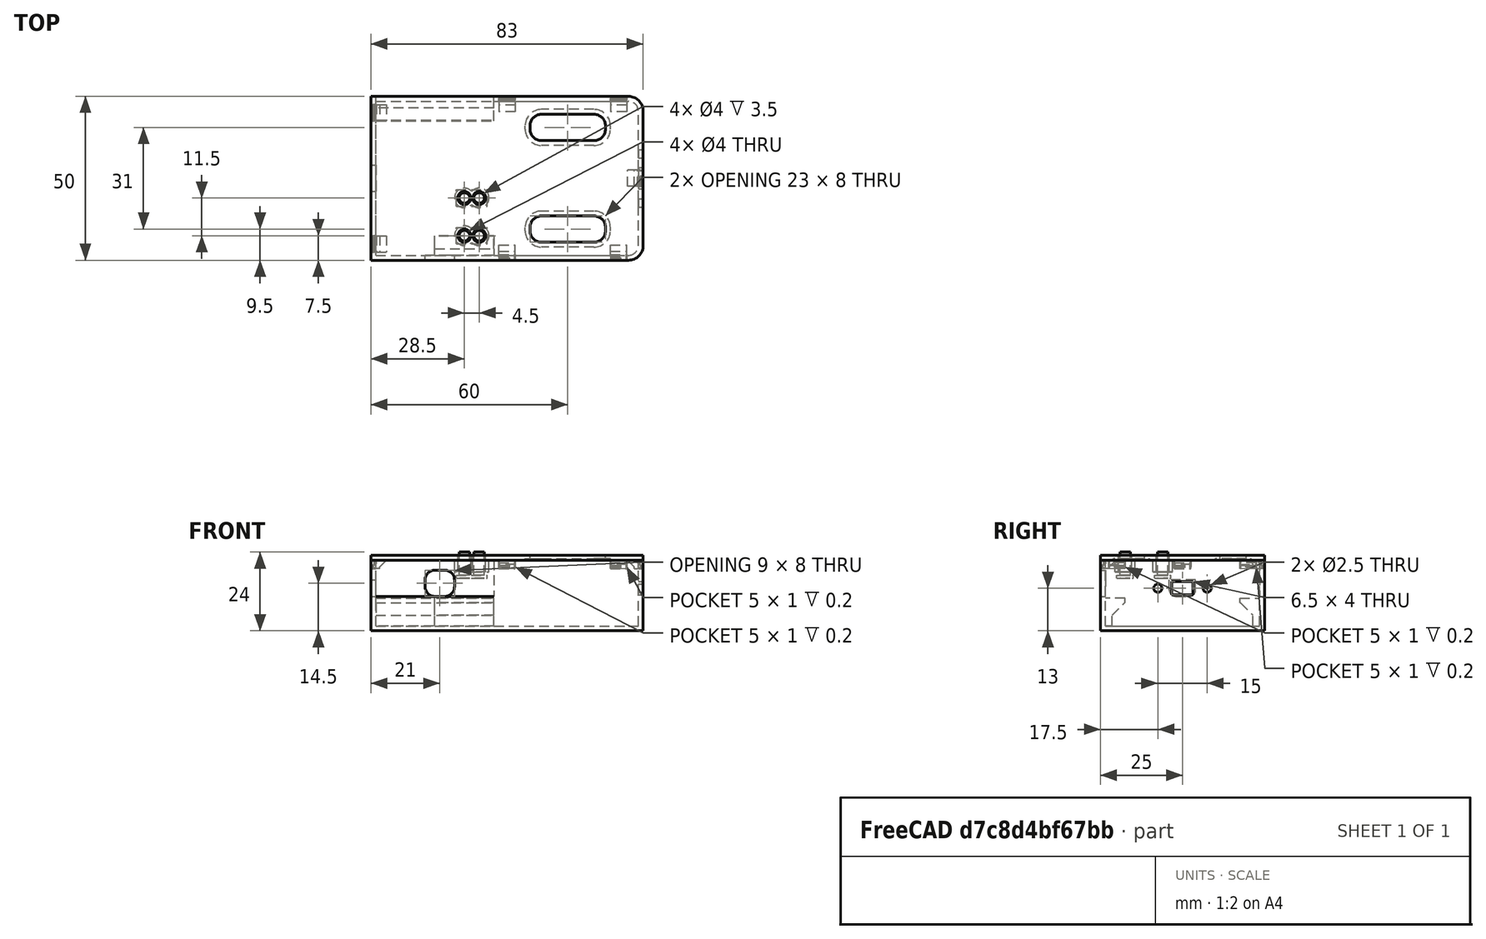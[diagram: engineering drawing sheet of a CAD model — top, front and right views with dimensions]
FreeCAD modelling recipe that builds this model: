
FCSTD DOCUMENT  (FreeCAD 0.19R24291 (Git))
Label: mp3-player
License: All rights reserved
LicenseURL: http://en.wikipedia.org/wiki/All_rights_reserved
objects: Part::Box×46, Part::Cut×36, Part::Chamfer×29, Part::Fuse×22, Part::Cylinder×18, Part::Fillet×16, Part::MultiFuse×1
note: 168 computed .brp shape members not serialized (recipe doc carries the construction recipe); baked Part::Feature solids carry a one-line shape summary decoded from their .brp

FEATURE [Part::Box] Box  label="Cube"
  AttacherType = Attacher::AttachEngine3D
  Height = 20
  Length = 80
  Placement = pos=(0,0,1.5) rot=(0,0,1;0rad)
  Width = 47
FEATURE [Part::Box] Box001  label="Cube001"
  AttacherType = Attacher::AttachEngine3D
  Height = 21.5
  Length = 83
  Placement = pos=(-1.5,-1.5,0) rot=(0,0,1;0rad)
  Width = 50
FEATURE [Part::Box] Box002  label="Cube002"
  AttacherType = Attacher::AttachEngine3D
  Height = 11
  Length = 36
  Placement = pos=(0,8,10.5) rot=(0,0,1;0rad)
  Width = 47
FEATURE [Part::Cut] Cut
  Base = -> Box001
  Tool = -> Box
FEATURE [Part::Fillet] Fillet
  Base = -> Cut
  Edges = 2 edges r=3: [Edge21,Edge22]
FEATURE [Part::Fillet] Fillet001
  Base = -> Fillet
  Edges = 2 edges r=4.5: [Edge27,Edge29]
FEATURE [Part::Box] Box003  label="Cube003"
  AttacherType = Attacher::AttachEngine3D
  Height = 5
  Length = 36
  Placement = pos=(-19,19.5,10.5) rot=(0,0,1;0rad)
  Width = 8
FEATURE [Part::Cut] Cut001
  Base = -> Fillet001
  Tool = -> Box002
FEATURE [Part::Cut] Cut002
  Base = -> Cut001
  Tool = -> Box003
FEATURE [Part::Fillet] Fillet002
  Base = -> Cut002
  Edges = 2 edges r=2: [Edge60,Edge61]
FEATURE [Part::Box] Box005  label="Cube005"
  AttacherType = Attacher::AttachEngine3D
  Height = 4
  Length = 10
  Placement = pos=(76,20.25,11) rot=(0,0,1;0rad)
  Width = 6.5
FEATURE [Part::Cylinder] Cylinder
  Angle = 360
  AttacherType = Attacher::AttachEngine3D
  Height = 10
  Placement = pos=(76,16,13) rot=(0,1,0;1.5708rad)
  Radius = 1.25
FEATURE [Part::Cylinder] Cylinder001
  Angle = 360
  AttacherType = Attacher::AttachEngine3D
  Height = 10
  Placement = pos=(76,31,13) rot=(0,1,0;1.5708rad)
  Radius = 1.25
FEATURE [Part::Cut] Cut003
  Base = -> Fillet002
  Tool = -> Cylinder
FEATURE [Part::Cut] Cut004
  Base = -> Cut003
  Tool = -> Cylinder001
FEATURE [Part::Cut] Cut005
  Base = -> Cut004
  Tool = -> Box005
FEATURE [Part::Box] Box006  label="Cube006"
  AttacherType = Attacher::AttachEngine3D
  Height = 1
  Length = 1
  Placement = pos=(-1,1,19) rot=(0,0,1;0rad)
  Width = 5
FEATURE [Part::Box] Box007  label="Cube007"
  AttacherType = Attacher::AttachEngine3D
  Height = 1
  Length = 1
  Placement = pos=(-1,41,19) rot=(0,0,1;0rad)
  Width = 5
FEATURE [Part::Box] Box008  label="Cube008"
  AttacherType = Attacher::AttachEngine3D
  Height = 1
  Length = 1
  Placement = pos=(80,21,19) rot=(0,0,1;0rad)
  Width = 5
FEATURE [Part::Box] Box009  label="Cube009"
  AttacherType = Attacher::AttachEngine3D
  Height = 1
  Length = 1
  Placement = pos=(37.5,1.1e-14,19) rot=(0,0,-1;1.5708rad)
  Width = 5
FEATURE [Part::Box] Box010  label="Cube010"
  AttacherType = Attacher::AttachEngine3D
  Height = 1
  Length = 1
  Placement = pos=(37.5,48,19) rot=(0,0,-1;1.5708rad)
  Width = 5
FEATURE [Part::Box] Box011  label="Cube011"
  AttacherType = Attacher::AttachEngine3D
  Height = 1
  Length = 1
  Placement = pos=(71.5,48,19) rot=(0,0,-1;1.5708rad)
  Width = 5
FEATURE [Part::Box] Box012  label="Cube012"
  AttacherType = Attacher::AttachEngine3D
  Height = 1
  Length = 1
  Placement = pos=(71.5,2.1e-14,19) rot=(0,0,-1;1.5708rad)
  Width = 5
FEATURE [Part::Box] Box013  label="Cube013"
  AttacherType = Attacher::AttachEngine3D
  Height = 3
  Length = 0.5
  Placement = pos=(71.5,2.1e-14,19) rot=(0,0,-1;1.5708rad)
  Width = 5
FEATURE [Part::Cut] Cut006
  Base = -> Cut005
  Tool = -> Box006
FEATURE [Part::Cut] Cut007
  Base = -> Cut006
  Tool = -> Box007
FEATURE [Part::Cut] Cut008
  Base = -> Cut007
  Tool = -> Box008
FEATURE [Part::Cut] Cut009
  Base = -> Cut008
  Tool = -> Box009
FEATURE [Part::Cut] Cut010
  Base = -> Cut009
  Tool = -> Box010
FEATURE [Part::Cut] Cut011
  Base = -> Cut010
  Tool = -> Box011
FEATURE [Part::Cut] Cut012
  Base = -> Cut011
  Tool = -> Box012
FEATURE [Part::Chamfer] Chamfer
  Base = -> Cut012
  Edges = 2 edges r=0.8: [Edge59,Edge79]
FEATURE [Part::Chamfer] Chamfer001
  Base = -> Chamfer
  Edges = 1 edges r=0.8: [Edge40]
FEATURE [Part::Chamfer] Chamfer002
  Base = -> Chamfer001
  Edges = 1 edges r=0.8: [Edge101]
FEATURE [Part::Chamfer] Chamfer003
  Base = -> Chamfer002
  Edges = 1 edges r=0.8: [Edge13]
FEATURE [Part::Chamfer] Chamfer004
  Base = -> Chamfer003
  Edges = 1 edges r=0.8: [Edge89]
FEATURE [Part::Chamfer] Chamfer005
  Base = -> Chamfer004
  Edges = 1 edges r=0.8: [Edge111]
FEATURE [Part::Box] Box015  label="Cube015"
  AttacherType = Attacher::AttachEngine3D
  Height = 3
  Length = 0.5
  Placement = pos=(37.5,1.3e-14,19) rot=(0,0,-1;1.5708rad)
  Width = 5
FEATURE [Part::Box] Box016  label="Cube016"
  AttacherType = Attacher::AttachEngine3D
  Height = 3
  Length = 0.5
  Placement = pos=(71.5,47.5,19) rot=(0,0,-1;1.5708rad)
  Width = 5
FEATURE [Part::Box] Box017  label="Cube017"
  AttacherType = Attacher::AttachEngine3D
  Height = 3
  Length = 0.5
  Placement = pos=(37.5,47.5,19) rot=(0,0,-1;1.5708rad)
  Width = 5
FEATURE [Part::Box] Box018  label="Cube018"
  AttacherType = Attacher::AttachEngine3D
  Height = 3
  Length = 0.5
  Placement = pos=(80,21,19) rot=(0,0,1;0rad)
  Width = 5
FEATURE [Part::Box] Box019  label="Cube019"
  AttacherType = Attacher::AttachEngine3D
  Height = 3
  Length = 0.5
  Placement = pos=(-0.5,41,19) rot=(0,0,1;0rad)
  Width = 5
FEATURE [Part::Box] Box020  label="Cube020"
  AttacherType = Attacher::AttachEngine3D
  Height = 3
  Length = 0.5
  Placement = pos=(-0.5,1,19) rot=(0,0,1;0rad)
  Width = 5
FEATURE [Part::Cut] Cut013
  Base = -> Chamfer005
  Tool = -> Box013
FEATURE [Part::Cut] Cut014
  Base = -> Cut013
  Tool = -> Box015
FEATURE [Part::Cut] Cut015
  Base = -> Cut014
  Tool = -> Box016
FEATURE [Part::Cut] Cut016
  Base = -> Cut015
  Tool = -> Box017
FEATURE [Part::Cut] Cut017
  Base = -> Cut016
  Tool = -> Box018
FEATURE [Part::Cut] Cut018
  Base = -> Cut017
  Tool = -> Box019
FEATURE [Part::Cut] Cut019
  Base = -> Cut018
  Tool = -> Box020
FEATURE [Part::Box] Box023  label="Cube023"
  AttacherType = Attacher::AttachEngine3D
  Height = 8
  Length = 9
  Placement = pos=(15,-6,10.5) rot=(0,0,1;0rad)
  Width = 47
FEATURE [Part::Cut] Cut020
  Base = -> Cut019
  Tool = -> Box023
FEATURE [Part::Fillet] Fillet003
  Base = -> Cut020
  Edges = 4 edges r=3: [Edge104,Edge105,Edge107,Edge109]
FEATURE [Part::Box] Box024  label="Cube024"
  AttacherType = Attacher::AttachEngine3D
  Height = 8.5
  Length = 36
  Placement = pos=(0,41,1.5) rot=(0,0,1;0rad)
  Width = 6
FEATURE [Part::Box] Box025  label="Cube025"
  AttacherType = Attacher::AttachEngine3D
  Height = 8.5
  Length = 36
  Placement = pos=(0,39,0) rot=(0,0,1;0rad)
  Width = 6
FEATURE [Part::Cut] Cut021
  Base = -> Box024
  Tool = -> Box025
FEATURE [Part::Box] Box026  label="Cube026"
  AttacherType = Attacher::AttachEngine3D
  Height = 8.5
  Length = 36
  Placement = pos=(0,41,1.5) rot=(0,0,1;0rad)
  Width = 6
FEATURE [Part::Box] Box027  label="Cube027"
  AttacherType = Attacher::AttachEngine3D
  Height = 8.5
  Length = 36
  Placement = pos=(0,39,0) rot=(0,0,1;0rad)
  Width = 6
FEATURE [Part::Cut] Cut022
  Base = -> Box026
  Placement = pos=(36,47,0) rot=(0,0,1;3.14159rad)
  Tool = -> Box027
FEATURE [Part::Box] Box028  label="Cube028"
  AttacherType = Attacher::AttachEngine3D
  Height = 11
  Length = 18
  Placement = pos=(0,-19.5,-0.5) rot=(0,0,1;0rad)
  Width = 47
FEATURE [Part::Cut] Cut023
  Base = -> Cut022
  Tool = -> Box028
FEATURE [Part::Box] Box014  label="Cube014"
  AttacherType = Attacher::AttachEngine3D
  Height = 0.8
  Length = 1
  Placement = pos=(71.5,0.2,19.1) rot=(0,0,-1;1.5708rad)
  Width = 5
FEATURE [Part::Box] Box029  label="Cube029"
  AttacherType = Attacher::AttachEngine3D
  Height = 1.5
  Length = 83
  Placement = pos=(-1.5,-1.5,21.5) rot=(0,0,1;0rad)
  Width = 50
FEATURE [Part::Fillet] Fillet004
  Base = -> Box029
  Edges = 2 edges r=4.5: [Edge5,Edge7]
FEATURE [Part::Box] Box030  label="Cube030"
  AttacherType = Attacher::AttachEngine3D
  Height = 3
  Length = 1
  Placement = pos=(71.5,1.2,19) rot=(0,0,-1;1.5708rad)
  Width = 5
FEATURE [Part::Fuse] Fusion
  Base = -> Box014
  Tool = -> Box030
FEATURE [Part::Chamfer] Chamfer006
  Base = -> Fusion
  Edges = 1 edges r=0.8: [Edge21]
FEATURE [Part::Chamfer] Chamfer007
  Base = -> Chamfer006
  Edges = 1 edges r=0.4: [Edge30]
FEATURE [Part::Box] Box031  label="Cube031"
  AttacherType = Attacher::AttachEngine3D
  Height = 3
  Length = 1
  Placement = pos=(71.5,1.2,19) rot=(0,0,-1;1.5708rad)
  Width = 5
FEATURE [Part::Box] Box032  label="Cube032"
  AttacherType = Attacher::AttachEngine3D
  Height = 0.8
  Length = 1
  Placement = pos=(71.5,0.2,19.1) rot=(0,0,-1;1.5708rad)
  Width = 5
FEATURE [Part::Fuse] Fusion001
  Base = -> Box032
  Tool = -> Box031
FEATURE [Part::Chamfer] Chamfer008
  Base = -> Fusion001
  Edges = 1 edges r=0.8: [Edge21]
FEATURE [Part::Chamfer] Chamfer009
  Base = -> Chamfer008
  Edges = 1 edges r=0.4: [Edge30]
  Placement = pos=(-34,0,0) rot=(0,0,1;0rad)
FEATURE [Part::Box] Box033  label="Cube033"
  AttacherType = Attacher::AttachEngine3D
  Height = 0.8
  Length = 1
  Placement = pos=(71.5,0.2,19.1) rot=(0,0,-1;1.5708rad)
  Width = 5
FEATURE [Part::Box] Box034  label="Cube034"
  AttacherType = Attacher::AttachEngine3D
  Height = 3
  Length = 1
  Placement = pos=(71.5,1.2,19) rot=(0,0,-1;1.5708rad)
  Width = 5
FEATURE [Part::Fuse] Fusion002
  Base = -> Box033
  Tool = -> Box034
FEATURE [Part::Chamfer] Chamfer010
  Base = -> Fusion002
  Edges = 1 edges r=0.8: [Edge21]
FEATURE [Part::Chamfer] Chamfer011
  Base = -> Chamfer010
  Edges = 1 edges r=0.4: [Edge30]
  Placement = pos=(114,47,0) rot=(0,0,1;3.14159rad)
FEATURE [Part::Box] Box035  label="Cube035"
  AttacherType = Attacher::AttachEngine3D
  Height = 3
  Length = 1
  Placement = pos=(71.5,1.2,19) rot=(0,0,-1;1.5708rad)
  Width = 5
FEATURE [Part::Box] Box036  label="Cube036"
  AttacherType = Attacher::AttachEngine3D
  Height = 0.8
  Length = 1
  Placement = pos=(71.5,0.2,19.1) rot=(0,0,-1;1.5708rad)
  Width = 5
FEATURE [Part::Fuse] Fusion003
  Base = -> Box036
  Tool = -> Box035
FEATURE [Part::Chamfer] Chamfer013
  Base = -> Fusion003
  Edges = 1 edges r=0.8: [Edge21]
FEATURE [Part::Chamfer] Chamfer012
  Base = -> Chamfer013
  Edges = 1 edges r=0.4: [Edge30]
  Placement = pos=(148,47,0) rot=(0,0,1;3.14159rad)
FEATURE [Part::Box] Box037  label="Cube037"
  AttacherType = Attacher::AttachEngine3D
  Height = 3
  Length = 1
  Placement = pos=(71.5,1.2,19) rot=(0,0,-1;1.5708rad)
  Width = 5
FEATURE [Part::Box] Box038  label="Cube038"
  AttacherType = Attacher::AttachEngine3D
  Height = 0.8
  Length = 1
  Placement = pos=(71.5,0.2,19.1) rot=(0,0,-1;1.5708rad)
  Width = 5
FEATURE [Part::Fuse] Fusion004
  Base = -> Box038
  Tool = -> Box037
FEATURE [Part::Chamfer] Chamfer015
  Base = -> Fusion004
  Edges = 1 edges r=0.8: [Edge21]
FEATURE [Part::Chamfer] Chamfer014
  Base = -> Chamfer015
  Edges = 1 edges r=0.4: [Edge30]
  Placement = pos=(80,-50.5,0) rot=(0,0,1;1.5708rad)
FEATURE [Part::Box] Box039  label="Cube039"
  AttacherType = Attacher::AttachEngine3D
  Height = 3
  Length = 1
  Placement = pos=(71.5,1.2,19) rot=(0,0,-1;1.5708rad)
  Width = 5
FEATURE [Part::Box] Box040  label="Cube040"
  AttacherType = Attacher::AttachEngine3D
  Height = 0.8
  Length = 1
  Placement = pos=(71.5,0.2,19.1) rot=(0,0,-1;1.5708rad)
  Width = 5
FEATURE [Part::Fuse] Fusion005
  Base = -> Box040
  Tool = -> Box039
FEATURE [Part::Chamfer] Chamfer017
  Base = -> Fusion005
  Edges = 1 edges r=0.8: [Edge21]
FEATURE [Part::Chamfer] Chamfer016
  Base = -> Chamfer017
  Edges = 1 edges r=0.4: [Edge30]
  Placement = pos=(2.9e-14,77.5,0) rot=(0,0,-1;1.5708rad)
FEATURE [Part::Box] Box041  label="Cube041"
  AttacherType = Attacher::AttachEngine3D
  Height = 3
  Length = 1
  Placement = pos=(71.5,1.2,19) rot=(0,0,-1;1.5708rad)
  Width = 5
FEATURE [Part::Box] Box042  label="Cube042"
  AttacherType = Attacher::AttachEngine3D
  Height = 0.8
  Length = 1
  Placement = pos=(71.5,0.2,19.1) rot=(0,0,-1;1.5708rad)
  Width = 5
FEATURE [Part::Fuse] Fusion006
  Base = -> Box042
  Tool = -> Box041
FEATURE [Part::Chamfer] Chamfer019
  Base = -> Fusion006
  Edges = 1 edges r=0.8: [Edge21]
FEATURE [Part::Chamfer] Chamfer018
  Base = -> Chamfer019
  Edges = 1 edges r=0.4: [Edge30]
  Placement = pos=(3e-15,117.5,0) rot=(0,0,-1;1.5708rad)
FEATURE [Part::Fuse] Fusion007
  Base = -> Fillet004
  Tool = -> Chamfer007
FEATURE [Part::Fuse] Fusion008
  Base = -> Fusion007
  Tool = -> Chamfer009
FEATURE [Part::Fuse] Fusion009
  Base = -> Fusion008
  Tool = -> Chamfer011
FEATURE [Part::Fuse] Fusion010
  Base = -> Fusion009
  Tool = -> Chamfer012
FEATURE [Part::Fuse] Fusion011
  Base = -> Fusion010
  Tool = -> Chamfer014
FEATURE [Part::Fuse] Fusion012
  Base = -> Fusion011
  Tool = -> Chamfer016
FEATURE [Part::Fuse] Fusion013
  Base = -> Fusion012
  Tool = -> Chamfer018
FEATURE [Part::Box] Box043  label="Cube043"
  AttacherType = Attacher::AttachEngine3D
  Height = 28
  Length = 26
  Placement = pos=(45.5,30.5,0) rot=(0,0,1;0rad)
  Width = 11
FEATURE [Part::Fillet] Fillet005
  Base = -> Box043
  Edges = 4 edges r=5: [Edge1,Edge3,Edge5,Edge7]
  Placement = pos=(0,3,-6) rot=(0,0,1;0rad)
FEATURE [Part::Box] Box044  label="Cube044"
  AttacherType = Attacher::AttachEngine3D
  Height = 28
  Length = 26
  Placement = pos=(45.5,30.5,0) rot=(0,0,1;0rad)
  Width = 11
FEATURE [Part::Fillet] Fillet006
  Base = -> Box044
  Edges = 4 edges r=5: [Edge1,Edge3,Edge5,Edge7]
  Placement = pos=(0,-28,-6) rot=(0,0,1;0rad)
FEATURE [Part::Box] Box045  label="Cube045"
  AttacherType = Attacher::AttachEngine3D
  Height = 28
  Length = 23
  Placement = pos=(47,35,0) rot=(0,0,1;0rad)
  Width = 8
FEATURE [Part::Box] Box046  label="Cube046"
  AttacherType = Attacher::AttachEngine3D
  Height = 28
  Length = 23
  Placement = pos=(47,4,0) rot=(0,0,1;0rad)
  Width = 8
FEATURE [Part::Cut] Cut024
  Base = -> Fusion013
  Tool = -> Fillet005
FEATURE [Part::Cut] Cut025
  Base = -> Cut024
  Tool = -> Fillet006
FEATURE [Part::Fillet] Fillet007
  Base = -> Box046
  Edges = 4 edges r=3.5: [Edge1,Edge3,Edge5,Edge7]
FEATURE [Part::Fillet] Fillet008
  Base = -> Box045
  Edges = 4 edges r=3.5: [Edge1,Edge3,Edge5,Edge7]
FEATURE [Part::Cut] Cut026
  Base = -> Cut025
  Tool = -> Fillet007
FEATURE [Part::Cut] Cut027
  Base = -> Cut026
  Tool = -> Fillet008
FEATURE [Part::Cylinder] Cylinder002
  Angle = 360
  AttacherType = Attacher::AttachEngine3D
  Height = 28
  Placement = pos=(27,17.5,0) rot=(0,0,1;0rad)
  Radius = 2
FEATURE [Part::Cylinder] Cylinder003
  Angle = 360
  AttacherType = Attacher::AttachEngine3D
  Height = 28
  Placement = pos=(31.5,17.5,0) rot=(0,0,1;0rad)
  Radius = 2
FEATURE [Part::Cylinder] Cylinder004
  Angle = 360
  AttacherType = Attacher::AttachEngine3D
  Height = 28
  Placement = pos=(31.5,6,0) rot=(0,0,1;0rad)
  Radius = 2
FEATURE [Part::Cylinder] Cylinder005
  Angle = 360
  AttacherType = Attacher::AttachEngine3D
  Height = 28
  Placement = pos=(27,6,0) rot=(0,0,1;0rad)
  Radius = 2
FEATURE [Part::Cut] Cut028
  Base = -> Cut027
  Tool = -> Cylinder002
FEATURE [Part::Cut] Cut029
  Base = -> Cut028
  Tool = -> Cylinder003
FEATURE [Part::Cut] Cut030
  Base = -> Cut029
  Tool = -> Cylinder004
FEATURE [Part::Cut] Cut031
  Base = -> Cut030
  Tool = -> Cylinder005
FEATURE [Part::Chamfer] Chamfer020
  Base = -> Cut031
  Edges = 1 edges r=2: [Edge39]
FEATURE [Part::Chamfer] Chamfer021
  Base = -> Chamfer020
  Edges = 1 edges r=2: [Edge39]
FEATURE [Part::Chamfer] Chamfer022
  Base = -> Chamfer021
  Edges = 1 edges r=2: [Edge53]
FEATURE [Part::Chamfer] Chamfer023
  Base = -> Chamfer022
  Edges = 1 edges r=2: [Edge31]
FEATURE [Part::Chamfer] Chamfer024
  Base = -> Chamfer023
  Edges = 1 edges r=2: [Edge45]
FEATURE [Part::Chamfer] Chamfer025
  Base = -> Chamfer024
  Edges = 1 edges r=2: [Edge63]
FEATURE [Part::Chamfer] Chamfer026
  Base = -> Chamfer025
  Edges = 1 edges r=2: [Edge57]
FEATURE [Part::Fillet] Fillet009
  Base = -> Chamfer026
  Edges = 2 edges r=0.4: [Edge318,Edge325]
FEATURE [Part::Fillet] Fillet010
  Base = -> Fillet009
  Edges = 2 edges r=0.4: [Edge325,Edge332]
FEATURE [Part::Fillet] Fillet011
  Base = -> Fillet010
  Edges = 2 edges r=0.4: [Edge297,Edge304]
FEATURE [Part::Fillet] Fillet012
  Base = -> Fillet011
  Edges = 2 edges r=0.4: [Edge283,Edge290]
FEATURE [Part::Fillet] Fillet013
  Base = -> Fillet012
  Edges = 2 edges r=0.4: [Edge255,Edge262]
FEATURE [Part::Fillet] Fillet014
  Base = -> Fillet013
  Edges = 2 edges r=0.4: [Edge255,Edge262]
FEATURE [Part::Fillet] Fillet015
  Base = -> Fillet014
  Edges = 2 edges r=0.4: [Edge291,Edge298]
FEATURE [Part::Cylinder] Cylinder006
  Angle = 360
  AttacherType = Attacher::AttachEngine3D
  Height = 8
  Placement = pos=(27,6,0) rot=(0,0,1;0rad)
  Radius = 1.6
FEATURE [Part::Cylinder] Cylinder007
  Angle = 360
  AttacherType = Attacher::AttachEngine3D
  Height = 8
  Placement = pos=(31.5,6,0) rot=(0,0,1;0rad)
  Radius = 1.6
FEATURE [Part::Box] Box047  label="Cube047"
  AttacherType = Attacher::AttachEngine3D
  Height = 1
  Length = 9.5
  Placement = pos=(24.5,3.5,0) rot=(0,0,1;0rad)
  Width = 5
FEATURE [Part::Fuse] Fusion014
  Base = -> Box047
  Tool = -> Cylinder006
FEATURE [Part::Fuse] Fusion015  label="Button_1"
  Base = -> Fusion014
  Placement = pos=(0,0,16) rot=(0,0,1;0rad)
  Tool = -> Cylinder007
FEATURE [Part::Cylinder] Cylinder008
  Angle = 360
  AttacherType = Attacher::AttachEngine3D
  Height = 3.5
  Placement = pos=(27,17.5,18) rot=(0,0,1;0rad)
  Radius = 2
FEATURE [Part::Cylinder] Cylinder009
  Angle = 360
  AttacherType = Attacher::AttachEngine3D
  Height = 3.5
  Placement = pos=(27,17.5,18) rot=(0,0,1;0rad)
  Radius = 3
FEATURE [Part::Cylinder] Cylinder010
  Angle = 360
  AttacherType = Attacher::AttachEngine3D
  Height = 3.5
  Placement = pos=(31.5,17.5,18) rot=(0,0,1;0rad)
  Radius = 2
FEATURE [Part::Cylinder] Cylinder011
  Angle = 360
  AttacherType = Attacher::AttachEngine3D
  Height = 3.5
  Placement = pos=(31.5,17.5,18) rot=(0,0,1;0rad)
  Radius = 3
FEATURE [Part::Cylinder] Cylinder012
  Angle = 360
  AttacherType = Attacher::AttachEngine3D
  Height = 3.5
  Placement = pos=(27,6,18) rot=(0,0,1;0rad)
  Radius = 2
FEATURE [Part::Cylinder] Cylinder013
  Angle = 360
  AttacherType = Attacher::AttachEngine3D
  Height = 3.5
  Placement = pos=(31.5,6,18) rot=(0,0,1;0rad)
  Radius = 2
FEATURE [Part::Cylinder] Cylinder014
  Angle = 360
  AttacherType = Attacher::AttachEngine3D
  Height = 3.5
  Placement = pos=(27,6,18) rot=(0,0,1;0rad)
  Radius = 3
FEATURE [Part::Cylinder] Cylinder015
  Angle = 360
  AttacherType = Attacher::AttachEngine3D
  Height = 3.5
  Placement = pos=(31.5,6,18) rot=(0,0,1;0rad)
  Radius = 3
FEATURE [Part::Fuse] Fusion016
  Base = -> Fillet015
  Tool = -> Cylinder009
FEATURE [Part::Fuse] Fusion017
  Base = -> Fusion016
  Tool = -> Cylinder011
FEATURE [Part::Fuse] Fusion018
  Base = -> Fusion017
  Tool = -> Cylinder014
FEATURE [Part::Fuse] Fusion019
  Base = -> Fusion018
  Tool = -> Cylinder015
FEATURE [Part::Cut] Cut032
  Base = -> Fusion019
  Tool = -> Cylinder008
FEATURE [Part::Cut] Cut033
  Base = -> Cut032
  Tool = -> Cylinder010
FEATURE [Part::Cut] Cut034
  Base = -> Cut033
  Tool = -> Cylinder012
FEATURE [Part::Cut] Cut035  label="Top"
  Base = -> Cut034
  Tool = -> Cylinder013
FEATURE [Part::Cylinder] Cylinder016
  Angle = 360
  AttacherType = Attacher::AttachEngine3D
  Height = 8
  Placement = pos=(27,6,0) rot=(0,0,1;0rad)
  Radius = 1.6
FEATURE [Part::Cylinder] Cylinder017
  Angle = 360
  AttacherType = Attacher::AttachEngine3D
  Height = 8
  Placement = pos=(31.5,6,0) rot=(0,0,1;0rad)
  Radius = 1.6
FEATURE [Part::Box] Box048  label="Cube048"
  AttacherType = Attacher::AttachEngine3D
  Height = 1
  Length = 9.5
  Placement = pos=(24.5,3.5,0) rot=(0,0,1;0rad)
  Width = 5
FEATURE [Part::Fuse] Fusion020
  Base = -> Box048
  Tool = -> Cylinder016
FEATURE [Part::Fuse] Fusion021  label="Button_2"
  Base = -> Fusion020
  Placement = pos=(0,11.5,16) rot=(0,0,1;0rad)
  Tool = -> Cylinder017
FEATURE [Part::MultiFuse] Fusion022
  Shapes = -> [Fillet003,Cut021,Cut023]
FEATURE [Part::Chamfer] Chamfer027
  Base = -> Fusion022
  Edges = 1 edges r=3.8: [Edge271]
FEATURE [Part::Chamfer] Chamfer028  label="Bottom"
  Base = -> Chamfer027
  Edges = 1 edges r=3.8: [Edge176]
